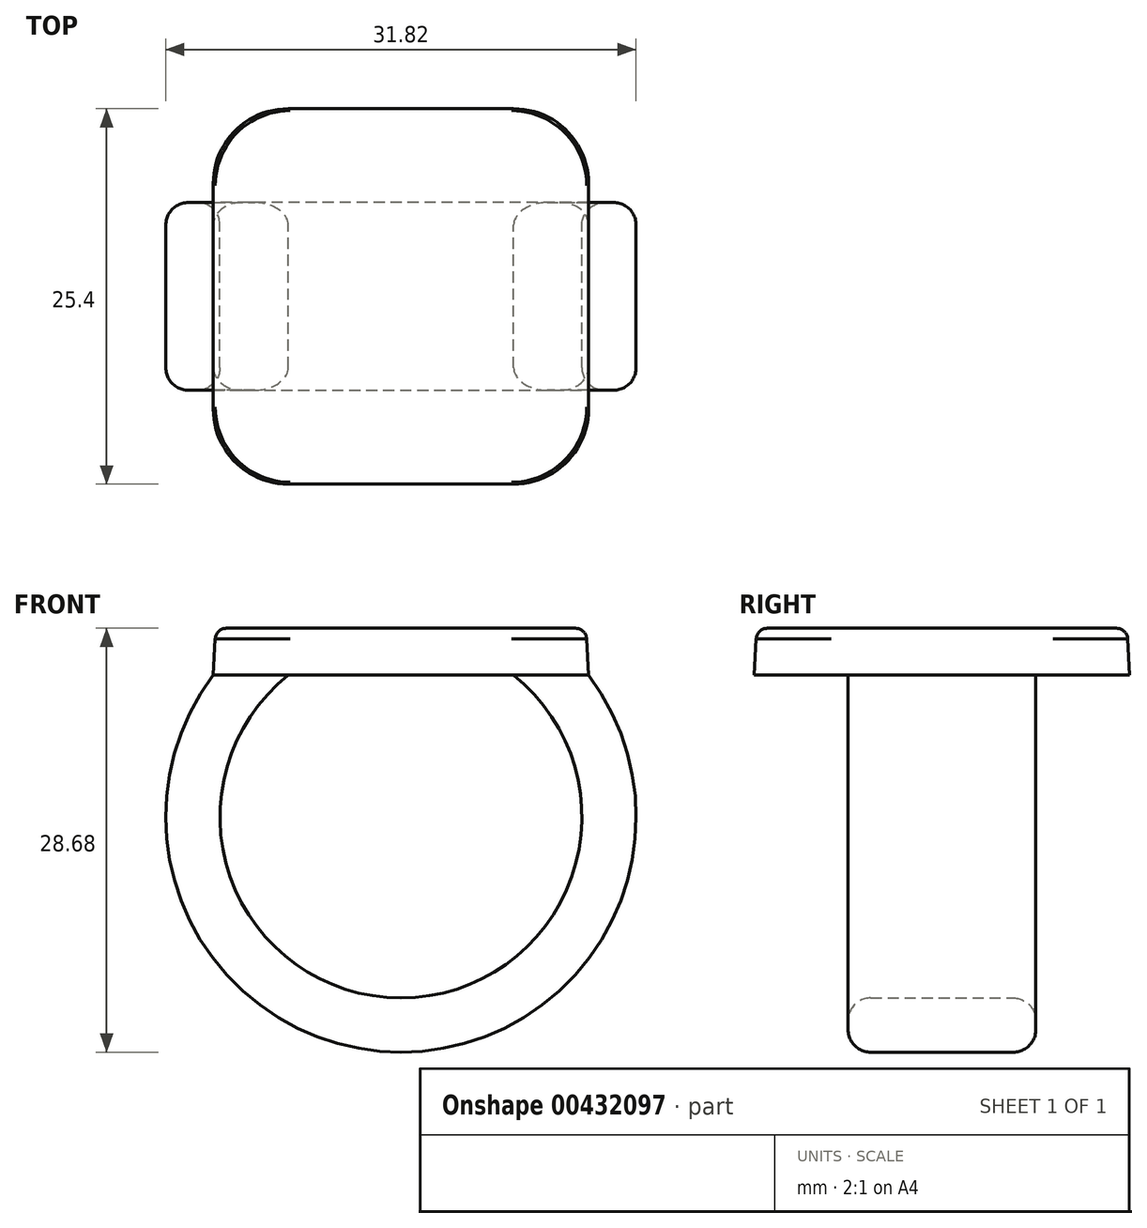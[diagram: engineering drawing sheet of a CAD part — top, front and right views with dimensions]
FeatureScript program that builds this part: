
annotation { "Feature Type Name" : "Feature", "Feature Type Description" : "" }
export const myFeature = defineFeature(function(context is Context, id is Id, definition is map)
    precondition{}
    {
        {
            var Q0;
            Q0=qCreatedBy(makeId("Top.planeOp"),FACE);
            var sketch = newSketch(context, id + "F0", { "sketchPlane" : qUnion([Q0])});
            skLineSegment(sketch, "E0.bottom", {"start": v(-12.7, 12.7) * mm, "end": v(12.7, 12.7) * mm});
            skLineSegment(sketch, "E0.top", {"start": v(-12.7, -12.7) * mm, "end": v(12.7, -12.7) * mm});
            skLineSegment(sketch, "E0.left", {"start": v(-12.7, 12.7) * mm, "end": v(-12.7, -12.7) * mm});
            skLineSegment(sketch, "E0.right", {"start": v(12.7, 12.7) * mm, "end": v(12.7, -12.7) * mm});
            skPoint(sketch, "E0.middle", {"position": v(0, 0) * mm});
            skSolve(sketch);
        }
        {
            var Q0;
            Q0 = qSketchRegion(id + "F0", true);
            extrude(context, id + "F1", {"entities" : qUnion([Q0]), "depth" : 3.17 * mm, "hasDraft" : true, "draftAngle" : 3 * degree, "draftPullDirection" : true});
        }
        {
            var Q0;
            Q0=qCreatedBy(makeId("Front.planeOp"),FACE);
            var sketch = newSketch(context, id + "F2", { "sketchPlane" : qUnion([Q0])});
            skArc(sketch, "E1", {"start": v(-10.16, 0) * mm, "mid": v(0, -23.56) * mm, "end": v(10.16, 0) * mm});
            skSolve(sketch);
        }
        {
            var Q0;
            Q0=makeQuery(id+"F1.opExtrude","CAP_FACE",FACE,{"disambiguationData":[OSD([sQuery(id+"F0.wireOp",EDGE,"E0.bottom"),sQuery(id+"F0.wireOp",EDGE,"E0.top"),sQuery(id+"F0.wireOp",EDGE,"E0.left"),sQuery(id+"F0.wireOp",EDGE,"E0.right")])],"isStart":true});
            var sketch = newSketch(context, id + "F3", { "sketchPlane" : qUnion([Q0])});
            skLineSegment(sketch, "E2.bottom", {"start": v(7.62, 6.35) * mm, "end": v(12.7, 6.35) * mm});
            skLineSegment(sketch, "E2.top", {"start": v(7.62, -6.35) * mm, "end": v(12.7, -6.35) * mm});
            skLineSegment(sketch, "E2.left", {"start": v(7.62, 6.35) * mm, "end": v(7.62, -6.35) * mm});
            skLineSegment(sketch, "E2.right", {"start": v(12.7, 6.35) * mm, "end": v(12.7, -6.35) * mm});
            skPoint(sketch, "E2.middle", {"position": v(10.16, 0) * mm});
            skSolve(sketch);
        }
        {
            var Q0;
            Q0 = qSketchRegion(id + "F3", true);
            var Q1;
            Q1 = qConstructionFilter(qBodyType(qCreatedBy(id + "F2" ,EDGE), BodyType.WIRE), ConstructionObject.NO);
            sweep(context, id + "F4", {"operationType" : NewBodyOperationType.ADD, "profiles" : qUnion([Q0]), "path" : qUnion([Q1])});
        }
        {
            var Q0;
            Q0=qCreatedBy(makeId("Front.planeOp"),FACE);
            var sketch = newSketch(context, id + "F5", { "sketchPlane" : qUnion([Q0])});
            skLineSegment(sketch, "E3.0", {"start": v(-10.16, 0) * mm, "end": v(-7.62, 0) * mm});
            skLineSegment(sketch, "E3.1", {"start": v(-10.16, 0) * mm, "end": v(-10.01, -2.54) * mm});
            skArc(sketch, "E3.2", {"start": v(-10.01, -2.54) * mm, "mid": v(-8.9, -1.18) * mm, "end": v(-7.62, 0) * mm});
            skPoint(sketch, "E4.orphan", {"position": v(-12.7, 0) * mm});
            skPoint(sketch, "E5.orphan", {"position": v(7.62, 0) * mm});
            skPoint(sketch, "E6.trimOffspring.end.orphan", {"position": v(12.7, 0) * mm});
            skSolve(sketch);
        }
        {
            var Q0;
            Q0 = qSketchRegion(id + "F5", true);
            var Q1;
            Q1=makeQuery(id+"F4.opSweep","SWEPT_FACE",FACE,{"disambiguationData":[OSD([sQuery(id+"F2.wireOp",EDGE,"E1"),sQuery(id+"F3.wireOp",EDGE,"E2.bottom")])]});
            var Q2;
            Q2=makeQuery(id+"F4.opSweep","SWEPT_FACE",FACE,{"disambiguationData":[OSD([sQuery(id+"F2.wireOp",EDGE,"E1"),sQuery(id+"F3.wireOp",EDGE,"E2.top")])]});
            extrude(context, id + "F6", {"entities" : qUnion([Q0]), "operationType" : NewBodyOperationType.ADD, "endBound" : BoundingType.UP_TO_SURFACE, "endBoundEntityFace" : qUnion([Q1]), "depth" : 25.4 * mm, "hasSecondDirection" : true, "secondDirectionBound" : SecondDirectionBoundingType.UP_TO_SURFACE, "secondDirectionOppositeDirection" : true, "secondDirectionBoundEntityFace" : qUnion([Q2]), "secondDirectionDepth" : 25.4 * mm});
        }
        {
            var Q0;
            Q0=makeQuery(id+"F1.opExtrude","SWEPT_EDGE",EDGE,{"disambiguationData":[OSD([sQuery(id+"F0.wireOp",EDGE,"E0.bottom"),sQuery(id+"F0.wireOp",EDGE,"E0.right")])]});
            var Q1;
            Q1=makeQuery(id+"F1.opExtrude","SWEPT_EDGE",EDGE,{"disambiguationData":[OSD([sQuery(id+"F0.wireOp",EDGE,"E0.bottom"),sQuery(id+"F0.wireOp",EDGE,"E0.left")])]});
            var Q2;
            Q2=makeQuery(id+"F1.opExtrude","SWEPT_EDGE",EDGE,{"disambiguationData":[OSD([sQuery(id+"F0.wireOp",EDGE,"E0.top"),sQuery(id+"F0.wireOp",EDGE,"E0.right")])]});
            var Q3;
            Q3=makeQuery(id+"F1.opExtrude","SWEPT_EDGE",EDGE,{"disambiguationData":[OSD([sQuery(id+"F0.wireOp",EDGE,"E0.top"),sQuery(id+"F0.wireOp",EDGE,"E0.left")])]});
            fillet(context, id + "F7", {"entities" : qUnion([Q0, Q1, Q2, Q3]), "radius" : 5.08 * mm, "tangentPropagation" : true, "allowEdgeOverflow" : false});
        }
        {
            var Q0;
            {var subQ0=sQuery(id+"F3.wireOp",EDGE,"E2.bottom");var subQ1=sQuery(id+"F2.wireOp",EDGE,"E1");Q0=makeQuery(id+"F6.boolean.opBoolean","MERGE",EDGE,{"derivedFrom":[makeQuery(id+"F4.opSweep","SWEPT_EDGE",EDGE,{"disambiguationData":[OSD([subQ1,subQ0,sQuery(id+"F3.wireOp",EDGE,"E2.left")])]}),makeQuery(id+"F6.opExtrude","TWEAK_EDGE",EDGE,{"derivedFrom":[makeQuery(id+"F4.opSweep","SWEPT_FACE",FACE,{"disambiguationData":[OSD([subQ1,subQ0])]}),makeQuery(id+"F5.imprint","IMPRINT",EDGE,{"derivedFrom":sQuery(id+"F5.wireOp",EDGE,"E3.2")})]})]});}
            var Q1;
            Q1=makeQuery(id+"F4.opSweep","SWEPT_EDGE",EDGE,{"disambiguationData":[OSD([sQuery(id+"F0.wireOp",EDGE,"E0.right"),sQuery(id+"F2.wireOp",EDGE,"E1"),sQuery(id+"F3.wireOp",EDGE,"E2.bottom"),sQuery(id+"F3.wireOp",EDGE,"E2.right")])]});
            var Q2;
            {var subQ0=sQuery(id+"F3.wireOp",EDGE,"E2.top");var subQ1=sQuery(id+"F2.wireOp",EDGE,"E1");Q2=makeQuery(id+"F6.boolean.opBoolean","MERGE",EDGE,{"derivedFrom":[makeQuery(id+"F4.opSweep","SWEPT_EDGE",EDGE,{"disambiguationData":[OSD([subQ1,subQ0,sQuery(id+"F3.wireOp",EDGE,"E2.left")])]}),makeQuery(id+"F6.opExtrude","TWEAK_EDGE",EDGE,{"derivedFrom":[makeQuery(id+"F4.opSweep","SWEPT_FACE",FACE,{"disambiguationData":[OSD([subQ1,subQ0])]}),makeQuery(id+"F5.imprint","IMPRINT",EDGE,{"derivedFrom":sQuery(id+"F5.wireOp",EDGE,"E3.2")})]})]});}
            var Q3;
            Q3=makeQuery(id+"F4.opSweep","SWEPT_EDGE",EDGE,{"disambiguationData":[OSD([sQuery(id+"F0.wireOp",EDGE,"E0.right"),sQuery(id+"F2.wireOp",EDGE,"E1"),sQuery(id+"F3.wireOp",EDGE,"E2.top"),sQuery(id+"F3.wireOp",EDGE,"E2.right")])]});
            fillet(context, id + "F8", {"entities" : qUnion([Q0, Q1, Q2, Q3]), "radius" : 1.52 * mm, "tangentPropagation" : true, "allowEdgeOverflow" : false});
        }
        {
            var Q0;
            Q0=makeQuery(id+"F1.opExtrude","CAP_FACE",FACE,{"disambiguationData":[OSD([sQuery(id+"F0.wireOp",EDGE,"E0.bottom"),sQuery(id+"F0.wireOp",EDGE,"E0.top"),sQuery(id+"F0.wireOp",EDGE,"E0.left"),sQuery(id+"F0.wireOp",EDGE,"E0.right")])],"isStart":false});
            fillet(context, id + "F9", {"entities" : qUnion([Q0]), "radius" : 0.76 * mm, "tangentPropagation" : true, "allowEdgeOverflow" : false});
        }
    });
